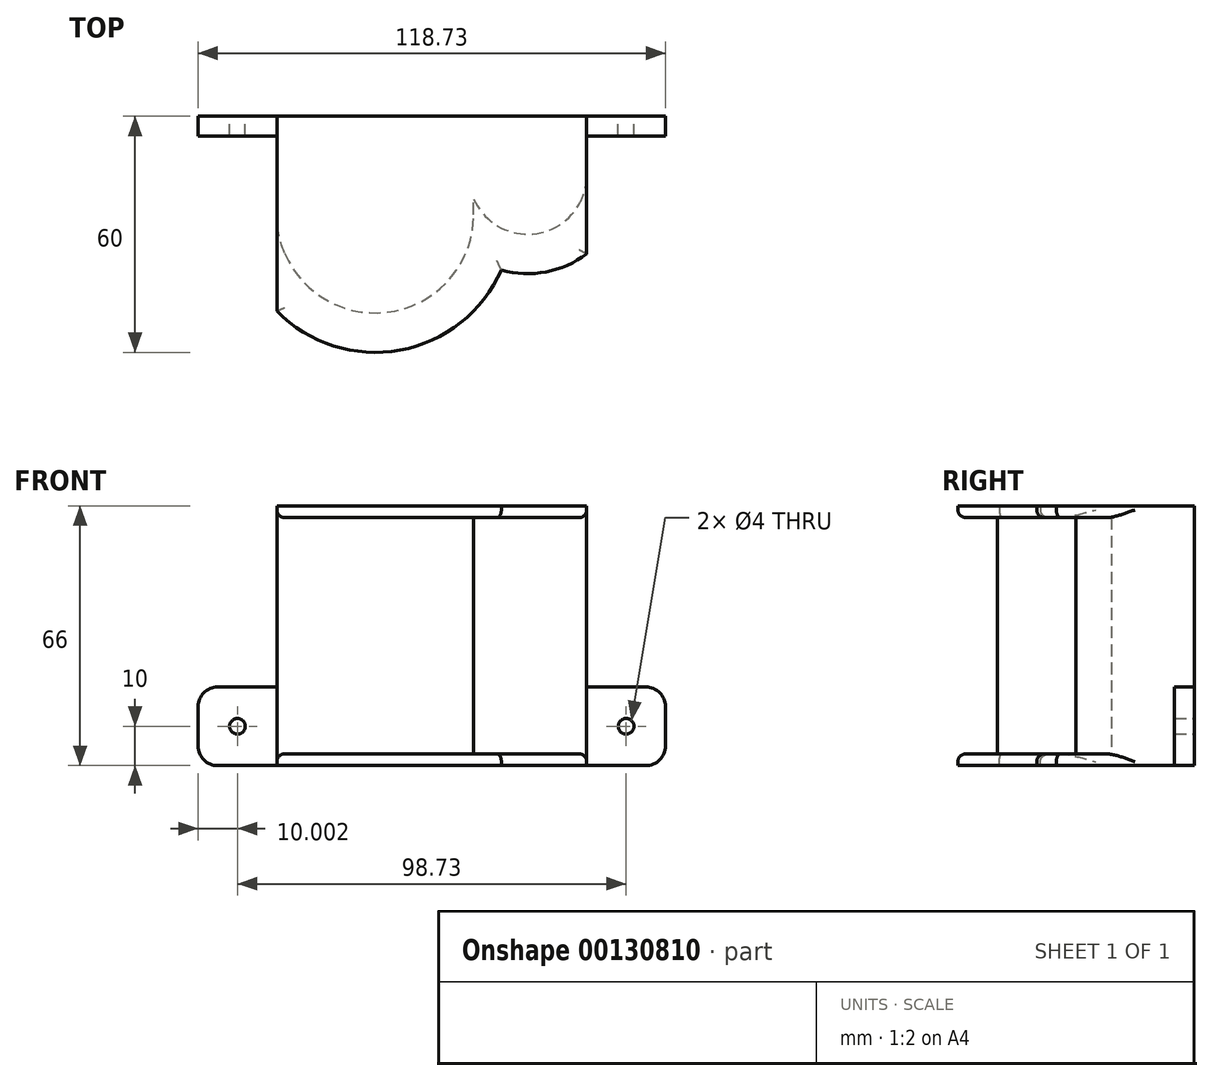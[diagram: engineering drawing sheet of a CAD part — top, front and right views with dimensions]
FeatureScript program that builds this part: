
annotation { "Feature Type Name" : "Feature", "Feature Type Description" : "" }
export const myFeature = defineFeature(function(context is Context, id is Id, definition is map)
    precondition{}
    {
        {
            var Q0;
            Q0=qCreatedBy(makeId("Top.planeOp"),FACE);
            var sketch = newSketch(context, id + "F0", { "sketchPlane" : qUnion([Q0])});
            skArc(sketch, "E0", {"start": v(-42.9, -21.2) * mm, "mid": v(-17.9, -46.2) * mm, "end": v(7.1, -21.2) * mm});
            skArc(sketch, "E1", {"start": v(7.1, -17.25) * mm, "mid": v(23.9, -25.88) * mm, "end": v(35.82, -11.2) * mm});
            skLineSegment(sketch, "E2.bottom", {"start": v(-42.9, 3.8) * mm, "end": v(35.82, 3.8) * mm});
            skLineSegment(sketch, "E3", {"start": v(35.82, -11.2) * mm, "end": v(35.82, 3.8) * mm});
            skPoint(sketch, "E3.endSnap0", {"position": v(-12.63, 3.8) * mm});
            skLineSegment(sketch, "E4", {"start": v(-42.9, -21.2) * mm, "end": v(-42.9, 3.8) * mm});
            skLineSegment(sketch, "E5", {"start": v(7.1, -21.2) * mm, "end": v(7.1, -17.25) * mm});
            skSolve(sketch);
        }
        {
            var Q0;
            Q0=makeQuery(id+"F0.imprint","IMPRINT",FACE,{"disambiguationData":[TD([[makeQuery(id+"F0.imprint","IMPRINT",EDGE,{"derivedFrom":sQuery(id+"F0.wireOp",EDGE,"E0")}),1.0]])]});
            extrude(context, id + "F1", {"entities" : qUnion([Q0]), "endBound" : BoundingType.SYMMETRIC, "depth" : 60 * mm});
        }
        {
            var Q0;
            Q0=makeQuery(id+"F1.opExtrude","CAP_FACE",FACE,{"disambiguationData":[OSD([sQuery(id+"F0.wireOp",EDGE,"E0"),sQuery(id+"F0.wireOp",EDGE,"E1"),sQuery(id+"F0.wireOp",EDGE,"E2.bottom"),sQuery(id+"F0.wireOp",EDGE,"E3"),sQuery(id+"F0.wireOp",EDGE,"E4"),sQuery(id+"F0.wireOp",EDGE,"E5")])],"isStart":false});
            var sketch = newSketch(context, id + "F2", { "sketchPlane" : qUnion([Q0])});
            skLineSegment(sketch, "E6.bottom", {"start": v(-42.9, 3.8) * mm, "end": v(35.82, 3.8) * mm});
            skLineSegment(sketch, "E6.left", {"start": v(-42.9, 3.8) * mm, "end": v(-42.9, -45.7) * mm});
            skLineSegment(sketch, "E6.right", {"start": v(35.82, 3.8) * mm, "end": v(35.82, -31.2) * mm});
            skLineSegment(sketch, "E7.bottom", {"start": v(35.82, 3.8) * mm, "end": v(35.82, 3.8) * mm});
            skLineSegment(sketch, "E7.top", {"start": v(35.82, 3.8) * mm, "end": v(35.82, 3.8) * mm});
            skLineSegment(sketch, "E7.left", {"start": v(35.82, 3.8) * mm, "end": v(35.82, 3.8) * mm});
            skLineSegment(sketch, "E7.right", {"start": v(35.82, 3.8) * mm, "end": v(35.82, 3.8) * mm});
            skArc(sketch, "E8", {"start": v(-42.9, -45.7) * mm, "mid": v(-11.63, -55.64) * mm, "end": v(14.13, -35.3) * mm});
            skArc(sketch, "E9", {"start": v(14.13, -35.3) * mm, "mid": v(25.45, -35.77) * mm, "end": v(35.82, -31.2) * mm});
            skArc(sketch, "E10.trimOffspring", {"start": v(-42.4, 3.8) * mm, "mid": v(-42.66, 3.54) * mm, "end": v(-42.9, 3.29) * mm});
            skSolve(sketch);
        }
        {
            var Q0;
            Q0=qSketchRegion(id+"F2",true);
            extrude(context, id + "F3", {"entities" : qUnion([Q0]), "operationType" : NewBodyOperationType.ADD, "depth" : 3 * mm});
        }
        {
            var Q0;
            Q0=makeQuery(id+"F1.opExtrude","CAP_FACE",FACE,{"disambiguationData":[OSD([sQuery(id+"F0.wireOp",EDGE,"E0"),sQuery(id+"F0.wireOp",EDGE,"E1"),sQuery(id+"F0.wireOp",EDGE,"E2.bottom"),sQuery(id+"F0.wireOp",EDGE,"E3"),sQuery(id+"F0.wireOp",EDGE,"E4"),sQuery(id+"F0.wireOp",EDGE,"E5")])],"isStart":true});
            var sketch = newSketch(context, id + "F4", { "sketchPlane" : qUnion([Q0])});
            skLineSegment(sketch, "E11", {"start": v(-42.9, 45.7) * mm, "end": v(-42.9, -3.8) * mm});
            skLineSegment(sketch, "E12", {"start": v(-42.9, -3.8) * mm, "end": v(35.82, -3.8) * mm});
            skLineSegment(sketch, "E13", {"start": v(35.82, -3.8) * mm, "end": v(35.82, 31.2) * mm});
            skArc(sketch, "E14.trimOffspring", {"start": v(14.13, 35.3) * mm, "mid": v(-11.63, 55.64) * mm, "end": v(-42.9, 45.7) * mm});
            skArc(sketch, "E15.trimOffspring", {"start": v(35.82, 31.2) * mm, "mid": v(25.45, 35.77) * mm, "end": v(14.13, 35.3) * mm});
            skSolve(sketch);
        }
        {
            var Q0;
            Q0=qSketchRegion(id+"F4",true);
            extrude(context, id + "F5", {"entities" : qUnion([Q0]), "operationType" : NewBodyOperationType.ADD, "depth" : 3 * mm});
        }
        {
            var Q0;
            Q0=makeQuery(id+"F5.boolean.opBoolean","MERGE",FACE,{"derivedFrom":[makeQuery(id+"F3.boolean.opBoolean","MERGE",FACE,{"derivedFrom":[makeQuery(id+"F1.opExtrude","SWEPT_FACE",FACE,{"disambiguationData":[OSD([sQuery(id+"F0.wireOp",EDGE,"E2.bottom")])]}),makeQuery(id+"F3.opExtrude","SWEPT_FACE",FACE,{"disambiguationData":[OSD([sQuery(id+"F2.wireOp",EDGE,"E6.bottom")])]})]}),makeQuery(id+"F5.opExtrude","SWEPT_FACE",FACE,{"disambiguationData":[OSD([sQuery(id+"F4.wireOp",EDGE,"E12")])]})]});
            var sketch = newSketch(context, id + "F6", { "sketchPlane" : qUnion([Q0])});
            skLineSegment(sketch, "E16.bottom", {"start": v(62.9, -33) * mm, "end": v(42.9, -33) * mm});
            skLineSegment(sketch, "E16.top", {"start": v(62.9, -13) * mm, "end": v(42.9, -13) * mm});
            skLineSegment(sketch, "E16.left", {"start": v(62.9, -33) * mm, "end": v(62.9, -13) * mm});
            skLineSegment(sketch, "E16.right", {"start": v(-55.82, -33) * mm, "end": v(-55.82, -13) * mm});
            skLineSegment(sketch, "E17", {"start": v(-35.82, -13) * mm, "end": v(-35.82, -33) * mm});
            skLineSegment(sketch, "E18", {"start": v(42.9, -33) * mm, "end": v(42.9, -13) * mm});
            skLineSegment(sketch, "E19.trimOffspring", {"start": v(-35.82, -13) * mm, "end": v(-55.82, -13) * mm});
            skLineSegment(sketch, "E20.trimOffspring", {"start": v(-35.82, -33) * mm, "end": v(-55.82, -33) * mm});
            skPoint(sketch, "E21.centerSnap0", {"position": v(-55.82, -23) * mm});
            skCircle(sketch, "E22", {"center": v(52.9, -23) * mm, "radius": 2 * mm});
            skPoint(sketch, "E22.centerSnap0", {"position": v(62.9, -23) * mm});
            skPoint(sketch, "E22.centerSnap1", {"position": v(52.9, -33) * mm});
            skCircle(sketch, "E23", {"center": v(-45.82, -23) * mm, "radius": 2 * mm});
            skPoint(sketch, "E23.centerSnap0", {"position": v(-45.82, -33) * mm});
            skSolve(sketch);
        }
        {
            var Q0;
            Q0=qSketchRegion(id+"F6",true);
            extrude(context, id + "F7", {"entities" : qUnion([Q0]), "operationType" : NewBodyOperationType.ADD, "oppositeDirection" : true, "depth" : 5 * mm});
        }
        {
            var Q0;
            Q0=makeQuery(id+"F7.opExtrude","CAP_EDGE",EDGE,{"disambiguationData":[OSD([sQuery(id+"F6.wireOp",EDGE,"E18")])],"isStart":false});
            var Q1;
            Q1=makeQuery(id+"F7.opExtrude","CAP_EDGE",EDGE,{"disambiguationData":[OSD([sQuery(id+"F6.wireOp",EDGE,"E17")])],"isStart":false});
            var Q2;
            Q2=makeQuery(id+"F7.opExtrude","SWEPT_EDGE",EDGE,{"disambiguationData":[OSD([sQuery(id+"F0.wireOp",EDGE,"E2.bottom"),sQuery(id+"F0.wireOp",EDGE,"E4"),sQuery(id+"F2.wireOp",EDGE,"E6.bottom"),sQuery(id+"F2.wireOp",EDGE,"E6.left"),sQuery(id+"F4.wireOp",EDGE,"E11"),sQuery(id+"F4.wireOp",EDGE,"E12"),sQuery(id+"F6.wireOp",EDGE,"E16.top"),sQuery(id+"F6.wireOp",EDGE,"E18")])]});
            var Q3;
            Q3=makeQuery(id+"F7.opExtrude","SWEPT_EDGE",EDGE,{"disambiguationData":[OSD([sQuery(id+"F0.wireOp",EDGE,"E2.bottom"),sQuery(id+"F0.wireOp",EDGE,"E3"),sQuery(id+"F2.wireOp",EDGE,"E6.bottom"),sQuery(id+"F2.wireOp",EDGE,"E6.right"),sQuery(id+"F4.wireOp",EDGE,"E12"),sQuery(id+"F4.wireOp",EDGE,"E13"),sQuery(id+"F6.wireOp",EDGE,"E17"),sQuery(id+"F6.wireOp",EDGE,"E19.trimOffspring")])]});
            var Q4;
            Q4=makeQuery(id+"F7.opExtrude","SWEPT_EDGE",EDGE,{"disambiguationData":[OSD([sQuery(id+"F6.wireOp",EDGE,"E16.right"),sQuery(id+"F6.wireOp",EDGE,"E19.trimOffspring")])]});
            var Q5;
            Q5=makeQuery(id+"F7.opExtrude","SWEPT_EDGE",EDGE,{"disambiguationData":[OSD([sQuery(id+"F6.wireOp",EDGE,"E16.right"),sQuery(id+"F6.wireOp",EDGE,"E20.trimOffspring")])]});
            var Q6;
            Q6=makeQuery(id+"F7.opExtrude","SWEPT_EDGE",EDGE,{"disambiguationData":[OSD([sQuery(id+"F6.wireOp",EDGE,"E16.bottom"),sQuery(id+"F6.wireOp",EDGE,"E16.left")])]});
            var Q7;
            Q7=makeQuery(id+"F7.opExtrude","SWEPT_EDGE",EDGE,{"disambiguationData":[OSD([sQuery(id+"F6.wireOp",EDGE,"E16.top"),sQuery(id+"F6.wireOp",EDGE,"E16.left")])]});
            fillet(context, id + "F8", {"entities" : qUnion([Q0, Q1, Q2, Q3, Q4, Q5, Q6, Q7]), "radius" : 5 * mm, "tangentPropagation" : true, "allowEdgeOverflow" : false});
        }
        {
            var Q0;
            Q0=makeQuery(id+"F3.opExtrude","CAP_EDGE",EDGE,{"disambiguationData":[OSD([sQuery(id+"F2.wireOp",EDGE,"E6.right")])],"isStart":true});
            var Q1;
            Q1=makeQuery(id+"F3.opExtrude","CAP_EDGE",EDGE,{"disambiguationData":[OSD([sQuery(id+"F2.wireOp",EDGE,"E9")])],"isStart":true});
            var Q2;
            Q2=makeQuery(id+"F3.opExtrude","CAP_EDGE",EDGE,{"disambiguationData":[OSD([sQuery(id+"F2.wireOp",EDGE,"E8")])],"isStart":true});
            var Q3;
            Q3=makeQuery(id+"F3.opExtrude","CAP_EDGE",EDGE,{"disambiguationData":[OSD([sQuery(id+"F2.wireOp",EDGE,"E6.left")])],"isStart":true});
            var Q4;
            Q4=makeQuery(id+"F1.opExtrude","CAP_EDGE",EDGE,{"disambiguationData":[OSD([sQuery(id+"F0.wireOp",EDGE,"E0")])],"isStart":false});
            var Q5;
            Q5=makeQuery(id+"F1.opExtrude","CAP_EDGE",EDGE,{"disambiguationData":[OSD([sQuery(id+"F0.wireOp",EDGE,"E1")])],"isStart":false});
            var Q6;
            Q6=makeQuery(id+"F5.opExtrude","CAP_EDGE",EDGE,{"disambiguationData":[OSD([sQuery(id+"F4.wireOp",EDGE,"E13")])],"isStart":true});
            var Q7;
            Q7=makeQuery(id+"F5.opExtrude","CAP_EDGE",EDGE,{"disambiguationData":[OSD([sQuery(id+"F4.wireOp",EDGE,"E15.trimOffspring")])],"isStart":true});
            var Q8;
            Q8=makeQuery(id+"F5.opExtrude","CAP_EDGE",EDGE,{"disambiguationData":[OSD([sQuery(id+"F4.wireOp",EDGE,"E14.trimOffspring")])],"isStart":true});
            var Q9;
            Q9=makeQuery(id+"F1.opExtrude","CAP_EDGE",EDGE,{"disambiguationData":[OSD([sQuery(id+"F0.wireOp",EDGE,"E0")])],"isStart":true});
            var Q10;
            Q10=makeQuery(id+"F5.opExtrude","CAP_EDGE",EDGE,{"disambiguationData":[OSD([sQuery(id+"F4.wireOp",EDGE,"E11")])],"isStart":true});
            var Q11;
            Q11=makeQuery(id+"F1.opExtrude","CAP_EDGE",EDGE,{"disambiguationData":[OSD([sQuery(id+"F0.wireOp",EDGE,"E1")])],"isStart":true});
            fillet(context, id + "F9", {"entities" : qUnion([Q0, Q1, Q2, Q3, Q4, Q5, Q6, Q7, Q8, Q9, Q10, Q11]), "radius" : 2 * mm, "tangentPropagation" : true, "allowEdgeOverflow" : false});
        }
    });
